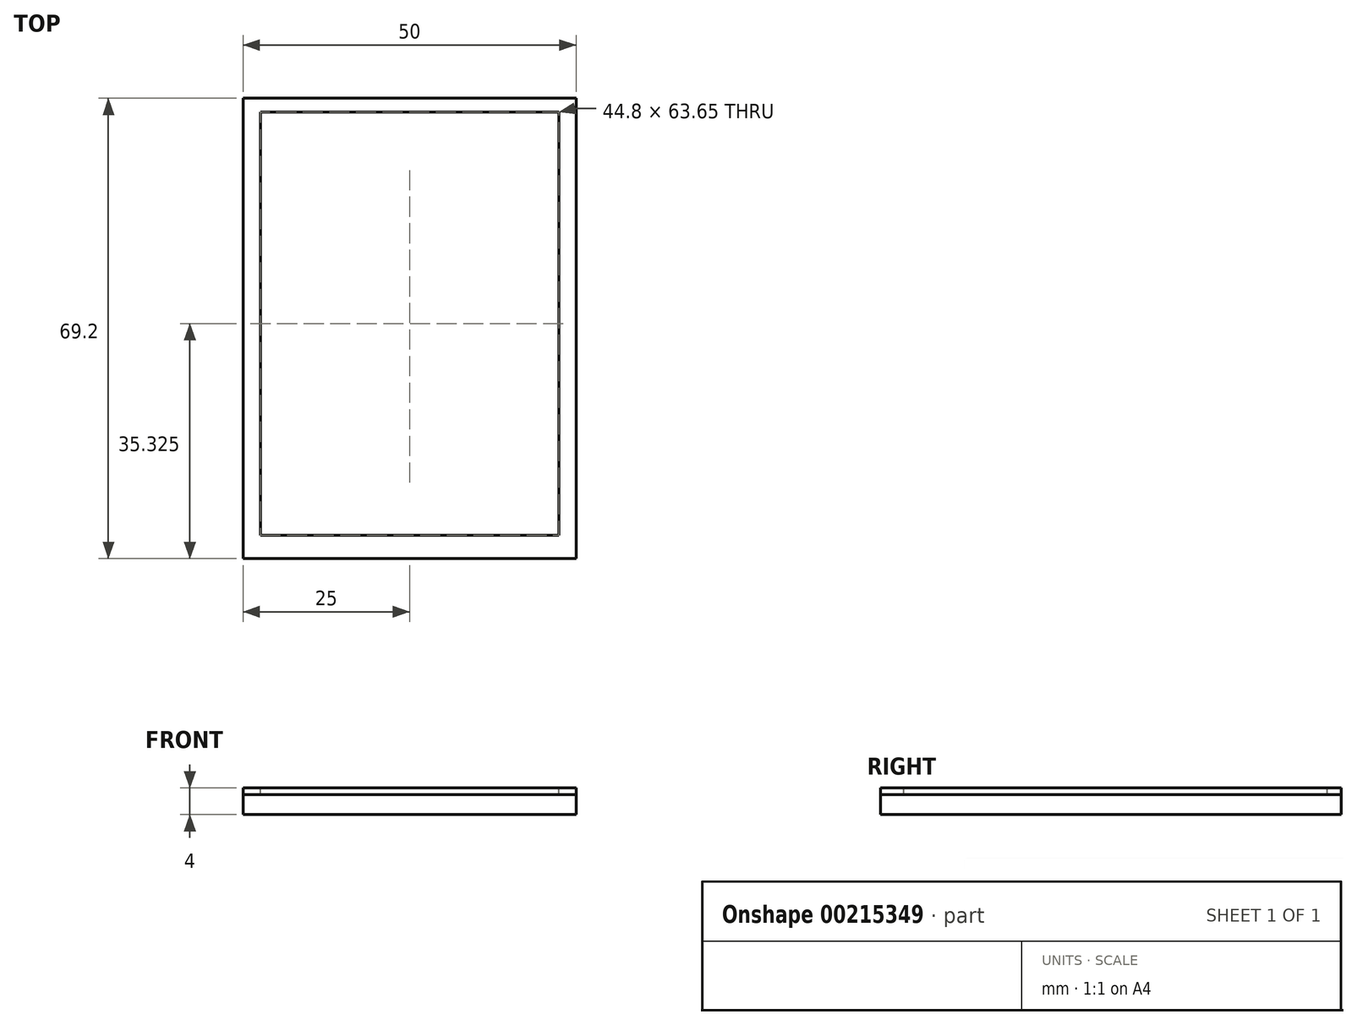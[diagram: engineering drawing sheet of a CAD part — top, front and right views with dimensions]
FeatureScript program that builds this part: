
annotation { "Feature Type Name" : "Feature", "Feature Type Description" : "" }
export const myFeature = defineFeature(function(context is Context, id is Id, definition is map)
    precondition{}
    {
        {
            var Q0;
            Q0=qCreatedBy(makeId("Top.planeOp"),FACE);
            var sketch = newSketch(context, id + "F0", { "sketchPlane" : qUnion([Q0])});
            skLineSegment(sketch, "E0.bottom", {"start": v(-25, 34.6) * mm, "end": v(25, 34.6) * mm});
            skLineSegment(sketch, "E0.top", {"start": v(-25, -34.6) * mm, "end": v(25, -34.6) * mm});
            skLineSegment(sketch, "E0.left", {"start": v(-25, 34.6) * mm, "end": v(-25, -34.6) * mm});
            skLineSegment(sketch, "E0.right", {"start": v(25, 34.6) * mm, "end": v(25, -34.6) * mm});
            skPoint(sketch, "E0.middle", {"position": v(0, 0) * mm});
            skSolve(sketch);
        }
        {
            var Q0;
            Q0 = qSketchRegion(id + "F0", true);
            extrude(context, id + "F1", {"entities" : qUnion([Q0]), "depth" : 3 * mm});
        }
        {
            var Q0;
            Q0=makeQuery(id+"F1.opExtrude","CAP_FACE",FACE,{"disambiguationData":[OSD([sQuery(id+"F0.wireOp",EDGE,"E0.bottom"),sQuery(id+"F0.wireOp",EDGE,"E0.top"),sQuery(id+"F0.wireOp",EDGE,"E0.left"),sQuery(id+"F0.wireOp",EDGE,"E0.right")])],"isStart":false});
            var sketch = newSketch(context, id + "F2", { "sketchPlane" : qUnion([Q0])});
            skLineSegment(sketch, "E1.bottom", {"start": v(-22.4, 32.55) * mm, "end": v(22.4, 32.55) * mm});
            skLineSegment(sketch, "E1.top", {"start": v(-22.4, -31.1) * mm, "end": v(22.4, -31.1) * mm});
            skLineSegment(sketch, "E1.left", {"start": v(-22.4, 32.55) * mm, "end": v(-22.4, -31.1) * mm});
            skLineSegment(sketch, "E1.right", {"start": v(22.4, 32.55) * mm, "end": v(22.4, -31.1) * mm});
            skLineSegment(sketch, "E2.bottom", {"start": v(-25, 34.6) * mm, "end": v(25, 34.6) * mm});
            skLineSegment(sketch, "E2.top", {"start": v(-25, -34.6) * mm, "end": v(25, -34.6) * mm});
            skLineSegment(sketch, "E2.left", {"start": v(-25, 34.6) * mm, "end": v(-25, -34.6) * mm});
            skLineSegment(sketch, "E2.right", {"start": v(25, 34.6) * mm, "end": v(25, -34.6) * mm});
            skSolve(sketch);
        }
        {
            var Q0;
            Q0 = qSketchRegion(id + "F2", true);
            extrude(context, id + "F3", {"entities" : qUnion([Q0]), "depth" : 1 * mm});
        }
        {
            var Q0;
            Q0=makeQuery(id+"F3.opExtrude","CAP_FACE",FACE,{"disambiguationData":[OSD([sQuery(id+"F2.wireOp",EDGE,"E1.bottom"),sQuery(id+"F2.wireOp",EDGE,"E1.top"),sQuery(id+"F2.wireOp",EDGE,"E1.left"),sQuery(id+"F2.wireOp",EDGE,"E1.right"),sQuery(id+"F2.wireOp",EDGE,"E2.bottom"),sQuery(id+"F2.wireOp",EDGE,"E2.top"),sQuery(id+"F2.wireOp",EDGE,"E2.left"),sQuery(id+"F2.wireOp",EDGE,"E2.right")])],"isStart":false});
            var sketch = newSketch(context, id + "F4", { "sketchPlane" : qUnion([Q0])});
            skLineSegment(sketch, "E3.bottom", {"start": v(-22.4, 32.55) * mm, "end": v(22.4, 32.55) * mm});
            skLineSegment(sketch, "E3.top", {"start": v(-22.4, -31.1) * mm, "end": v(22.4, -31.1) * mm});
            skLineSegment(sketch, "E3.left", {"start": v(-22.4, 32.55) * mm, "end": v(-22.4, -31.1) * mm});
            skLineSegment(sketch, "E3.right", {"start": v(22.4, 32.55) * mm, "end": v(22.4, -31.1) * mm});
            skSolve(sketch);
        }
        {
            var Q0;
            Q0 = qSketchRegion(id + "F4", true);
            extrude(context, id + "F5", {"entities" : qUnion([Q0]), "oppositeDirection" : true, "depth" : 1 * mm});
        }
    });
